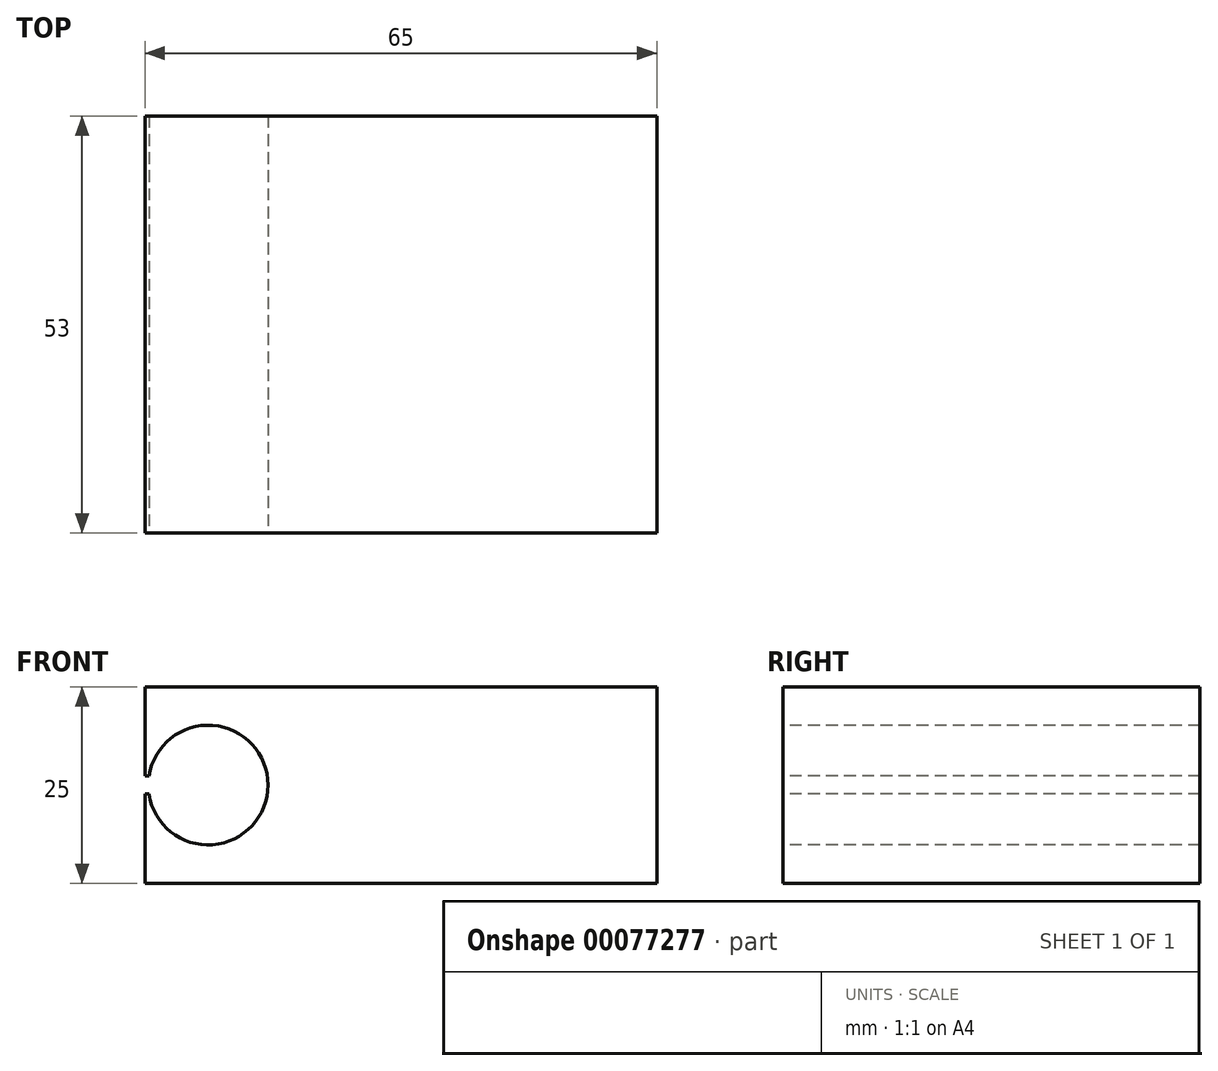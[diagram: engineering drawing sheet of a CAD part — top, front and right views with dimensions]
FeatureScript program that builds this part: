
annotation { "Feature Type Name" : "Feature", "Feature Type Description" : "" }
export const myFeature = defineFeature(function(context is Context, id is Id, definition is map)
    precondition{}
    {
        {
            var Q0;
            Q0=qCreatedBy(makeId("Top.planeOp"),FACE);
            var sketch = newSketch(context, id + "F0", { "sketchPlane" : qUnion([Q0])});
            skLineSegment(sketch, "E0.bottom", {"start": v(0, 0) * mm, "end": v(65, 0) * mm});
            skLineSegment(sketch, "E0.top", {"start": v(0, 53) * mm, "end": v(65, 53) * mm});
            skLineSegment(sketch, "E0.left", {"start": v(0, 0) * mm, "end": v(0, 53) * mm});
            skLineSegment(sketch, "E0.right", {"start": v(65, 0) * mm, "end": v(65, 53) * mm});
            skSolve(sketch);
        }
        {
            var Q0;
            Q0=qSketchRegion(id+"F0",true);
            extrude(context, id + "F1", {"entities" : qUnion([Q0]), "depth" : 25 * mm});
        }
        {
            var Q0;
            Q0=makeQuery(id+"F1.opExtrude","SWEPT_FACE",FACE,{"disambiguationData":[OSD([sQuery(id+"F0.wireOp",EDGE,"E0.bottom")])]});
            var sketch = newSketch(context, id + "F2", { "sketchPlane" : qUnion([Q0])});
            skCircle(sketch, "E1", {"center": v(8, 12.5) * mm, "radius": 7.6 * mm});
            skPoint(sketch, "E1.centerSnap0", {"position": v(0, 12.5) * mm});
            skLineSegment(sketch, "E2.bottom", {"start": v(0, 13.64) * mm, "end": v(0.49, 13.64) * mm});
            skLineSegment(sketch, "E2.top", {"start": v(0, 11.36) * mm, "end": v(0.49, 11.36) * mm});
            skLineSegment(sketch, "E2.left", {"start": v(0, 11.36) * mm, "end": v(0, 13.64) * mm});
            skLineSegment(sketch, "E2.right", {"start": v(0.49, 11.36) * mm, "end": v(0.49, 13.64) * mm});
            skPoint(sketch, "E3", {"position": v(0.49, 12.5) * mm});
            skSolve(sketch);
        }
        {
            var Q0;
            Q0=qSketchRegion(id+"F2",true);
            extrude(context, id + "F3", {"entities" : qUnion([Q0]), "operationType" : NewBodyOperationType.REMOVE, "endBound" : BoundingType.THROUGH_ALL, "oppositeDirection" : true, "depth" : 25 * mm});
        }
    });
